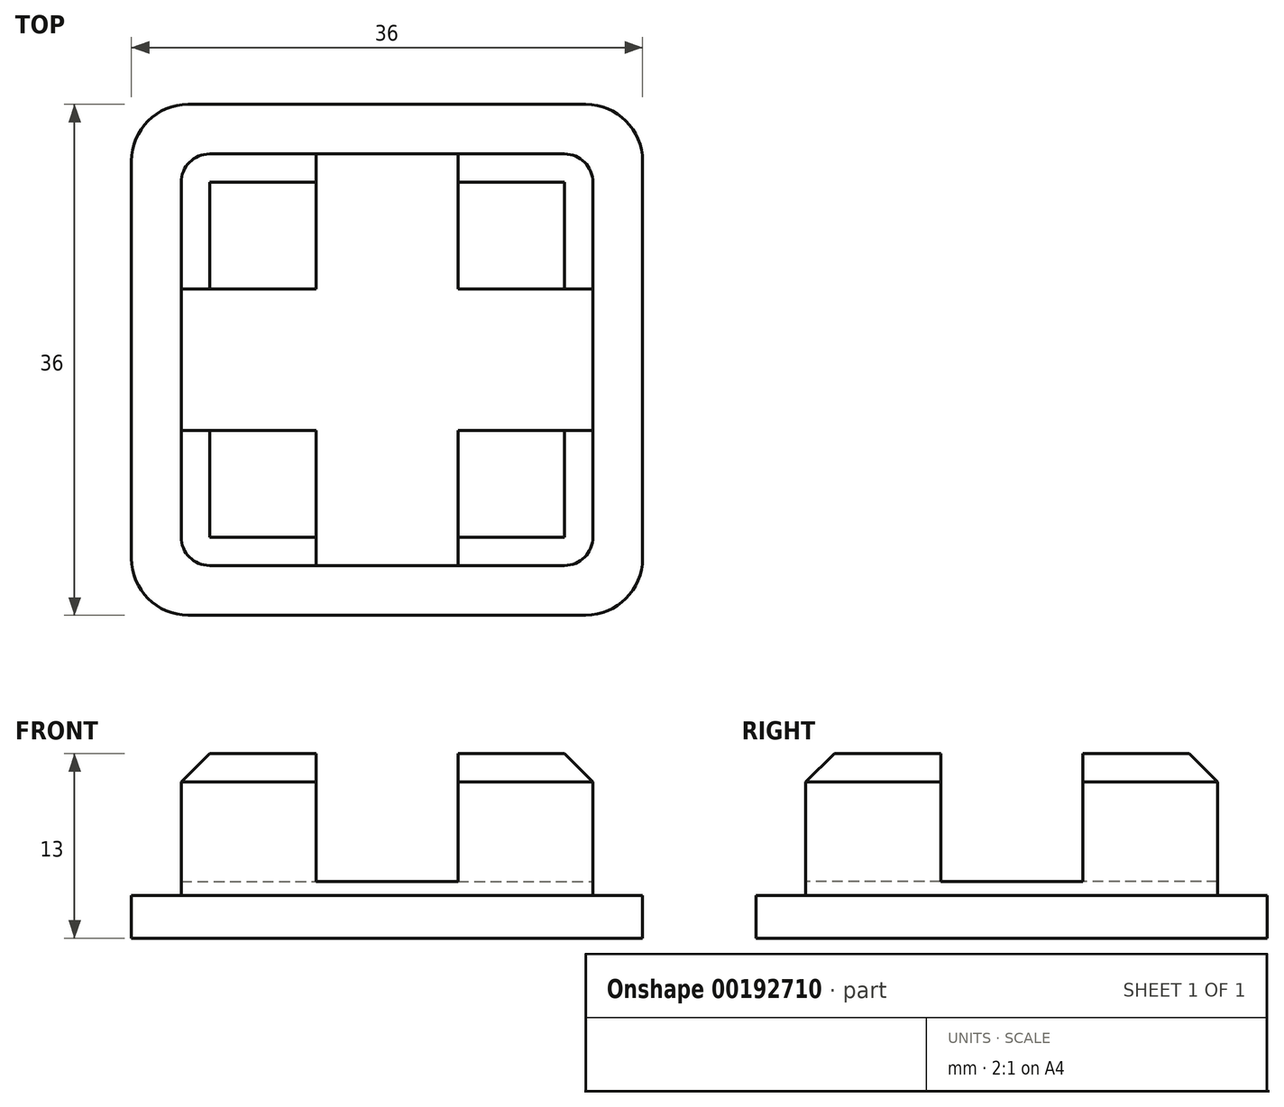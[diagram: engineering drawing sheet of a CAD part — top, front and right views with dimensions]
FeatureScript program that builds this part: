
annotation { "Feature Type Name" : "Feature", "Feature Type Description" : "" }
export const myFeature = defineFeature(function(context is Context, id is Id, definition is map)
    precondition{}
    {
        {
            var Q0;
            Q0=qCreatedBy(makeId("Top.planeOp"),FACE);
            var sketch = newSketch(context, id + "F0", { "sketchPlane" : qUnion([Q0])});
            skLineSegment(sketch, "E0.bottom", {"start": v(-11.6, 18.48) * mm, "end": v(16.4, 18.48) * mm});
            skLineSegment(sketch, "E0.top", {"start": v(-11.6, -17.52) * mm, "end": v(16.4, -17.52) * mm});
            skLineSegment(sketch, "E0.left", {"start": v(-15.6, 14.48) * mm, "end": v(-15.6, -13.52) * mm});
            skLineSegment(sketch, "E0.right", {"start": v(20.4, 14.48) * mm, "end": v(20.4, -13.52) * mm});
            skPoint(sketch, "E1.visualSharp", {"position": v(-15.6, 18.48) * mm});
            skArc(sketch, "E1.filletArc", {"start": v(-11.6, 18.48) * mm, "mid": v(-14.44, 17.31) * mm, "end": v(-15.6, 14.48) * mm});
            skPoint(sketch, "E2.visualSharp", {"position": v(-15.6, -17.52) * mm});
            skArc(sketch, "E2.filletArc", {"start": v(-15.6, -13.52) * mm, "mid": v(-14.44, -16.34) * mm, "end": v(-11.6, -17.52) * mm});
            skPoint(sketch, "E3.visualSharp", {"position": v(20.4, -17.52) * mm});
            skArc(sketch, "E3.filletArc", {"start": v(16.4, -17.52) * mm, "mid": v(19.22, -16.34) * mm, "end": v(20.4, -13.52) * mm});
            skPoint(sketch, "E4.visualSharp", {"position": v(20.4, 18.48) * mm});
            skArc(sketch, "E4.filletArc", {"start": v(20.4, 14.48) * mm, "mid": v(19.22, 17.31) * mm, "end": v(16.4, 18.48) * mm});
            skSolve(sketch);
        }
        {
            var Q0;
            Q0=makeQuery(id+"F0.imprint","IMPRINT",FACE,{"disambiguationData":[TD([[makeQuery(id+"F0.imprint","IMPRINT",EDGE,{"derivedFrom":sQuery(id+"F0.wireOp",EDGE,"E0.bottom")}),-1.0]])]});
            extrude(context, id + "F1", {"entities" : qUnion([Q0]), "depth" : 3 * mm});
        }
        {
            var Q0;
            Q0=makeQuery(id+"F1.opExtrude","CAP_FACE",FACE,{"disambiguationData":[OSD([sQuery(id+"F0.wireOp",EDGE,"E0.bottom"),sQuery(id+"F0.wireOp",EDGE,"E0.top"),sQuery(id+"F0.wireOp",EDGE,"E0.left"),sQuery(id+"F0.wireOp",EDGE,"E0.right"),sQuery(id+"F0.wireOp",EDGE,"E1.filletArc"),sQuery(id+"F0.wireOp",EDGE,"E2.filletArc"),sQuery(id+"F0.wireOp",EDGE,"E3.filletArc"),sQuery(id+"F0.wireOp",EDGE,"E4.filletArc")])],"isStart":false});
            var sketch = newSketch(context, id + "F2", { "sketchPlane" : qUnion([Q0])});
            skLineSegment(sketch, "E5.bottom", {"start": v(-10.1, 14.98) * mm, "end": v(14.9, 14.98) * mm});
            skLineSegment(sketch, "E5.top", {"start": v(-10.1, -14.02) * mm, "end": v(14.9, -14.02) * mm});
            skLineSegment(sketch, "E5.left", {"start": v(-12.1, 12.98) * mm, "end": v(-12.1, -12.02) * mm});
            skLineSegment(sketch, "E5.right", {"start": v(16.9, 12.98) * mm, "end": v(16.9, -12.02) * mm});
            skPoint(sketch, "E6.visualSharp", {"position": v(-12.1, 14.98) * mm});
            skArc(sketch, "E6.filletArc", {"start": v(-10.1, 14.98) * mm, "mid": v(-11.52, 14.4) * mm, "end": v(-12.1, 12.98) * mm});
            skPoint(sketch, "E7.visualSharp", {"position": v(-12.1, -14.02) * mm});
            skArc(sketch, "E7.filletArc", {"start": v(-12.1, -12.02) * mm, "mid": v(-11.52, -13.43) * mm, "end": v(-10.1, -14.02) * mm});
            skPoint(sketch, "E8.visualSharp", {"position": v(16.9, -14.02) * mm});
            skArc(sketch, "E8.filletArc", {"start": v(14.9, -14.02) * mm, "mid": v(16.3, -13.43) * mm, "end": v(16.9, -12.02) * mm});
            skPoint(sketch, "E9.visualSharp", {"position": v(16.9, 14.98) * mm});
            skArc(sketch, "E9.filletArc", {"start": v(16.9, 12.98) * mm, "mid": v(16.3, 14.4) * mm, "end": v(14.9, 14.98) * mm});
            skSolve(sketch);
        }
        {
            var Q0;
            Q0=makeQuery(id+"F2.imprint","IMPRINT",FACE,{"disambiguationData":[TD([[makeQuery(id+"F2.imprint","IMPRINT",EDGE,{"derivedFrom":sQuery(id+"F2.wireOp",EDGE,"E5.bottom")}),-1.0]])]});
            extrude(context, id + "F3", {"entities" : qUnion([Q0]), "operationType" : NewBodyOperationType.ADD, "depth" : 10 * mm});
        }
        {
            var Q0;
            Q0=makeQuery(id+"F3.opExtrude","CAP_FACE",FACE,{"disambiguationData":[OSD([sQuery(id+"F2.wireOp",EDGE,"E5.bottom"),sQuery(id+"F2.wireOp",EDGE,"E5.top"),sQuery(id+"F2.wireOp",EDGE,"E5.left"),sQuery(id+"F2.wireOp",EDGE,"E5.right"),sQuery(id+"F2.wireOp",EDGE,"E6.filletArc"),sQuery(id+"F2.wireOp",EDGE,"E7.filletArc"),sQuery(id+"F2.wireOp",EDGE,"E8.filletArc"),sQuery(id+"F2.wireOp",EDGE,"E9.filletArc")])],"isStart":false});
            var sketch = newSketch(context, id + "F4", { "sketchPlane" : qUnion([Q0])});
            skLineSegment(sketch, "E10.0", {"start": v(-2.6, 14.98) * mm, "end": v(-2.6, 5.48) * mm});
            skLineSegment(sketch, "E11.0", {"start": v(7.4, 14.98) * mm, "end": v(7.4, 5.48) * mm});
            skLineSegment(sketch, "E12.0", {"start": v(-12.1, -4.52) * mm, "end": v(-2.6, -4.52) * mm});
            skLineSegment(sketch, "E13.0", {"start": v(-12.1, 5.48) * mm, "end": v(-2.6, 5.48) * mm});
            skLineSegment(sketch, "E14", {"start": v(-12.1, 5.48) * mm, "end": v(-12.1, -4.52) * mm});
            skLineSegment(sketch, "E15", {"start": v(16.9, 5.48) * mm, "end": v(16.9, -4.52) * mm});
            skLineSegment(sketch, "E16", {"start": v(-2.6, -14.02) * mm, "end": v(7.4, -14.02) * mm});
            skLineSegment(sketch, "E17", {"start": v(-2.6, 14.98) * mm, "end": v(7.4, 14.98) * mm});
            skLineSegment(sketch, "E18.trimOffspring", {"start": v(-2.6, -4.52) * mm, "end": v(-2.6, -14.02) * mm});
            skLineSegment(sketch, "E19.trimOffspring", {"start": v(7.4, 5.48) * mm, "end": v(16.9, 5.48) * mm});
            skLineSegment(sketch, "E20.trimOffspring", {"start": v(7.4, -4.52) * mm, "end": v(7.4, -14.02) * mm});
            skLineSegment(sketch, "E21.trimOffspring", {"start": v(7.4, -4.52) * mm, "end": v(16.9, -4.52) * mm});
            skSolve(sketch);
        }
        {
            var Q0;
            Q0=makeQuery(id+"F4.imprint","IMPRINT",FACE,{"disambiguationData":[TD([[makeQuery(id+"F4.imprint","IMPRINT",EDGE,{"derivedFrom":sQuery(id+"F4.wireOp",EDGE,"E10.0")}),1.0]])]});
            extrude(context, id + "F5", {"entities" : qUnion([Q0]), "operationType" : NewBodyOperationType.REMOVE, "oppositeDirection" : true, "depth" : 9 * mm});
        }
        {
            var Q0;
            {var subQ0=sQuery(id+"F2.wireOp",EDGE,"E8.filletArc");var subQ1=sQuery(id+"F2.wireOp",EDGE,"E5.top");Q0=makeQuery(id+"F5.boolean.opBoolean","SPLIT",EDGE,{"disambiguationData":[TD([makeQuery(id+"F3.opExtrude","SWEPT_FACE",FACE,{"disambiguationData":[OSD([subQ0])]})])],"derivedFrom":makeQuery(id+"F3.opExtrude","CAP_EDGE",EDGE,{"disambiguationData":[OSD([subQ1])],"isStart":false})});}
            var Q1;
            {var subQ0=sQuery(id+"F2.wireOp",EDGE,"E7.filletArc");var subQ1=sQuery(id+"F2.wireOp",EDGE,"E5.top");Q1=makeQuery(id+"F5.boolean.opBoolean","SPLIT",EDGE,{"disambiguationData":[TD([makeQuery(id+"F3.opExtrude","SWEPT_FACE",FACE,{"disambiguationData":[OSD([subQ0])]})])],"derivedFrom":makeQuery(id+"F3.opExtrude","CAP_EDGE",EDGE,{"disambiguationData":[OSD([subQ1])],"isStart":false})});}
            var Q2;
            {var subQ0=sQuery(id+"F2.wireOp",EDGE,"E9.filletArc");var subQ1=sQuery(id+"F2.wireOp",EDGE,"E5.right");Q2=makeQuery(id+"F5.boolean.opBoolean","SPLIT",EDGE,{"disambiguationData":[TD([makeQuery(id+"F3.opExtrude","SWEPT_FACE",FACE,{"disambiguationData":[OSD([subQ0])]})])],"derivedFrom":makeQuery(id+"F3.opExtrude","CAP_EDGE",EDGE,{"disambiguationData":[OSD([subQ1])],"isStart":false})});}
            var Q3;
            {var subQ0=sQuery(id+"F2.wireOp",EDGE,"E6.filletArc");var subQ1=sQuery(id+"F2.wireOp",EDGE,"E5.left");Q3=makeQuery(id+"F5.boolean.opBoolean","SPLIT",EDGE,{"disambiguationData":[TD([makeQuery(id+"F3.opExtrude","SWEPT_FACE",FACE,{"disambiguationData":[OSD([subQ0])]})])],"derivedFrom":makeQuery(id+"F3.opExtrude","CAP_EDGE",EDGE,{"disambiguationData":[OSD([subQ1])],"isStart":false})});}
            chamfer(context, id + "F6", {"entities" : qUnion([Q0, Q1, Q2, Q3]), "width" : 2 * mm, "tangentPropagation" : true});
        }
    });
